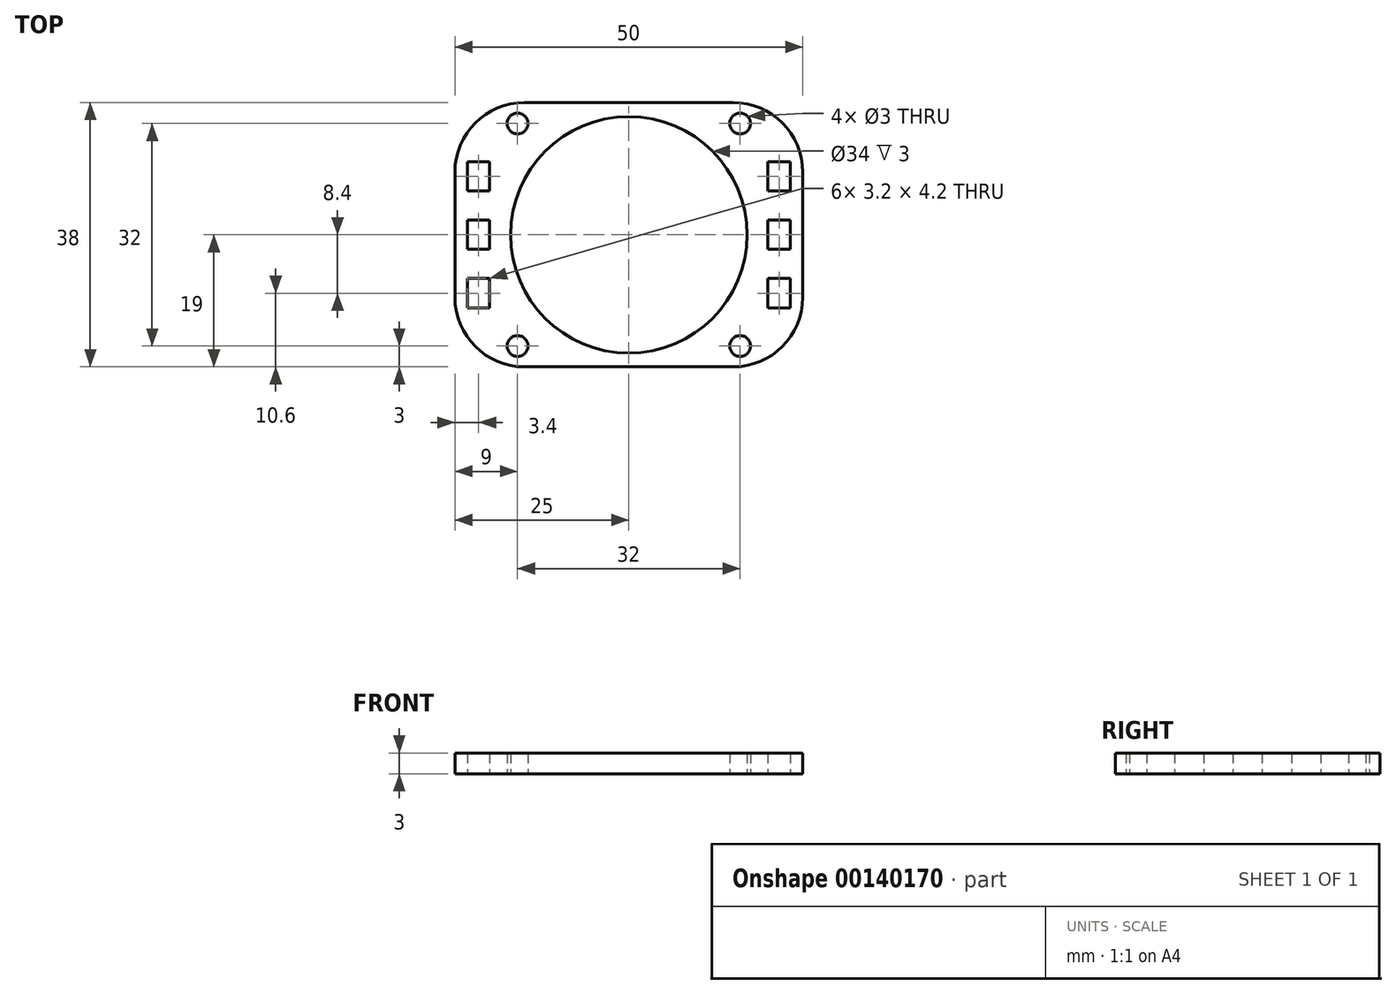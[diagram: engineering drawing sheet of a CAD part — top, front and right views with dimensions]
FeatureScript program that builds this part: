
annotation { "Feature Type Name" : "Feature", "Feature Type Description" : "" }
export const myFeature = defineFeature(function(context is Context, id is Id, definition is map)
    precondition{}
    {
        {
            var Q0;
            Q0=qCreatedBy(makeId("Top.planeOp"),FACE);
            var sketch = newSketch(context, id + "F0", { "sketchPlane" : qUnion([Q0])});
            skCircle(sketch, "E0", {"center": v(0, 0) * mm, "radius": 17 * mm});
            skLineSegment(sketch, "E1.bottom", {"start": v(-15, 19) * mm, "end": v(15, 19) * mm});
            skLineSegment(sketch, "E1.top", {"start": v(-15, -19) * mm, "end": v(15, -19) * mm});
            skLineSegment(sketch, "E1.left", {"start": v(-25, 9) * mm, "end": v(-25, -9) * mm});
            skLineSegment(sketch, "E1.right", {"start": v(25, 9) * mm, "end": v(25, -9) * mm});
            skLineSegment(sketch, "E2", {"start": v(17, 0) * mm, "end": v(25, 0) * mm, "construction": true});
            skLineSegment(sketch, "E3", {"start": v(25, -19) * mm, "end": v(25, -14) * mm, "construction": true});
            skLineSegment(sketch, "E4", {"start": v(25, -14) * mm, "end": v(25, -9) * mm, "construction": true});
            skLineSegment(sketch, "E5", {"start": v(25, -9) * mm, "end": v(25, -4) * mm, "construction": true});
            skLineSegment(sketch, "E6", {"start": v(25, -4) * mm, "end": v(25, 1) * mm, "construction": true});
            skLineSegment(sketch, "E7", {"start": v(25, 1) * mm, "end": v(25, 6) * mm, "construction": true});
            skLineSegment(sketch, "E8", {"start": v(25, 6) * mm, "end": v(25, 11) * mm, "construction": true});
            skLineSegment(sketch, "E9", {"start": v(25, -19) * mm, "end": v(19, -19) * mm, "construction": true});
            skLineSegment(sketch, "E10", {"start": v(19, -19) * mm, "end": v(19, 19) * mm, "construction": true});
            skLineSegment(sketch, "E11", {"start": v(0, 19) * mm, "end": v(0, -19) * mm, "construction": true});
            skLineSegment(sketch, "E12", {"start": v(-25, 0) * mm, "end": v(25, 0) * mm, "construction": true});
            skLineSegment(sketch, "E13", {"start": v(0, 19) * mm, "end": v(-16, 19) * mm, "construction": true});
            skLineSegment(sketch, "E14", {"start": v(-16, 19) * mm, "end": v(-16, 16) * mm, "construction": true});
            skCircle(sketch, "E15", {"center": v(-16, 16) * mm, "radius": 1.5 * mm});
            skCircle(sketch, "E16.MirrorC", {"center": v(16, 16) * mm, "radius": 1.5 * mm});
            skCircle(sketch, "E17.MirrorC", {"center": v(16, -16) * mm, "radius": 1.5 * mm});
            skCircle(sketch, "E18.MirrorC", {"center": v(-16, -16) * mm, "radius": 1.5 * mm});
            skLineSegment(sketch, "E19", {"start": v(22.2, 19) * mm, "end": v(22.2, -19) * mm, "construction": true});
            skLineSegment(sketch, "E20", {"start": v(0, 19) * mm, "end": v(-20, 19) * mm, "construction": true});
            skLineSegment(sketch, "E21", {"start": v(-20, 19) * mm, "end": v(-20, -19) * mm, "construction": true});
            skLineSegment(sketch, "E22", {"start": v(-20, -19) * mm, "end": v(-23.2, -19) * mm, "construction": true});
            skLineSegment(sketch, "E23", {"start": v(-23.2, -19) * mm, "end": v(-23.2, 19) * mm, "construction": true});
            skLineSegment(sketch, "E24", {"start": v(19, 10.5) * mm, "end": v(-23.2, 10.5) * mm, "construction": true});
            skLineSegment(sketch, "E25", {"start": v(22.2, 2.1) * mm, "end": v(-23.2, 2.1) * mm, "construction": true});
            skLineSegment(sketch, "E26", {"start": v(22.2, -6.3) * mm, "end": v(-23.2, -6.3) * mm, "construction": true});
            skLineSegment(sketch, "E27", {"start": v(-23.2, 2.1) * mm, "end": v(-23.2, 0) * mm});
            skLineSegment(sketch, "E28", {"start": v(-20, 10.5) * mm, "end": v(-20, 6.3) * mm});
            skLineSegment(sketch, "E29", {"start": v(-20, 6.3) * mm, "end": v(-23.2, 6.3) * mm});
            skLineSegment(sketch, "E30", {"start": v(-23.2, 6.3) * mm, "end": v(-23.2, 10.5) * mm});
            skLineSegment(sketch, "E31", {"start": v(-23.2, 10.5) * mm, "end": v(-20, 10.5) * mm});
            skLineSegment(sketch, "E32", {"start": v(-20, 2.1) * mm, "end": v(-20, -2.1) * mm});
            skLineSegment(sketch, "E33", {"start": v(-20, -2.1) * mm, "end": v(-23.2, -2.1) * mm});
            skLineSegment(sketch, "E34", {"start": v(-23.2, -2.1) * mm, "end": v(-23.2, 2.1) * mm});
            skLineSegment(sketch, "E35", {"start": v(-20, 2.1) * mm, "end": v(-23.2, 2.1) * mm});
            skLineSegment(sketch, "E36", {"start": v(-20, -6.3) * mm, "end": v(-20, -10.5) * mm});
            skLineSegment(sketch, "E37", {"start": v(-20, -10.5) * mm, "end": v(-23.2, -10.5) * mm});
            skLineSegment(sketch, "E38", {"start": v(-23.2, -10.5) * mm, "end": v(-23.2, -6.3) * mm});
            skLineSegment(sketch, "E39", {"start": v(-20, -6.3) * mm, "end": v(-23.2, -6.3) * mm});
            skLineSegment(sketch, "E40.MirrorCS", {"start": v(23.2, 2.1) * mm, "end": v(23.2, 0) * mm});
            skLineSegment(sketch, "E41.MirrorCS", {"start": v(23.2, -2.1) * mm, "end": v(23.2, 2.1) * mm});
            skLineSegment(sketch, "E42.MirrorCS", {"start": v(20, 2.1) * mm, "end": v(20, -2.1) * mm});
            skLineSegment(sketch, "E43.MirrorCS", {"start": v(23.2, 10.5) * mm, "end": v(20, 10.5) * mm});
            skLineSegment(sketch, "E44.MirrorCS", {"start": v(23.2, -10.5) * mm, "end": v(23.2, -6.3) * mm});
            skLineSegment(sketch, "E45.MirrorCS", {"start": v(20, -6.3) * mm, "end": v(20, -10.5) * mm});
            skLineSegment(sketch, "E46.MirrorCS", {"start": v(23.2, 6.3) * mm, "end": v(23.2, 10.5) * mm});
            skLineSegment(sketch, "E47.MirrorCS", {"start": v(20, -10.5) * mm, "end": v(23.2, -10.5) * mm});
            skLineSegment(sketch, "E48.MirrorCS", {"start": v(20, 6.3) * mm, "end": v(23.2, 6.3) * mm});
            skLineSegment(sketch, "E49.MirrorCS", {"start": v(20, 2.1) * mm, "end": v(23.2, 2.1) * mm});
            skLineSegment(sketch, "E50.MirrorCS", {"start": v(20, 10.5) * mm, "end": v(20, 6.3) * mm});
            skLineSegment(sketch, "E51.MirrorCS", {"start": v(20, -6.3) * mm, "end": v(23.2, -6.3) * mm});
            skLineSegment(sketch, "E52.MirrorCS", {"start": v(20, -2.1) * mm, "end": v(23.2, -2.1) * mm});
            skPoint(sketch, "E53.visualSharp", {"position": v(25, 19) * mm});
            skArc(sketch, "E53.filletArc", {"start": v(25, 9) * mm, "mid": v(22.07, 16.07) * mm, "end": v(15, 19) * mm});
            skPoint(sketch, "E54.visualSharp", {"position": v(-25, 19) * mm});
            skArc(sketch, "E54.filletArc", {"start": v(-15, 19) * mm, "mid": v(-22.07, 16.07) * mm, "end": v(-25, 9) * mm});
            skPoint(sketch, "E55.visualSharp", {"position": v(-25, -19) * mm});
            skArc(sketch, "E55.filletArc", {"start": v(-25, -9) * mm, "mid": v(-22.07, -16.07) * mm, "end": v(-15, -19) * mm});
            skPoint(sketch, "E56.visualSharp", {"position": v(25, -19) * mm});
            skArc(sketch, "E56.filletArc", {"start": v(15, -19) * mm, "mid": v(22.07, -16.07) * mm, "end": v(25, -9) * mm});
            skSolve(sketch);
        }
        {
            var Q0;
            Q0=makeQuery(id+"F0.imprint","IMPRINT",FACE,{"disambiguationData":[TD([[makeQuery(id+"F0.imprint","IMPRINT",EDGE,{"derivedFrom":sQuery(id+"F0.wireOp",EDGE,"E0")}),-1.0]])]});
            extrude(context, id + "F1", {"entities" : qUnion([Q0]), "endBound" : BoundingType.SYMMETRIC, "depth" : 3 * mm});
        }
    });
